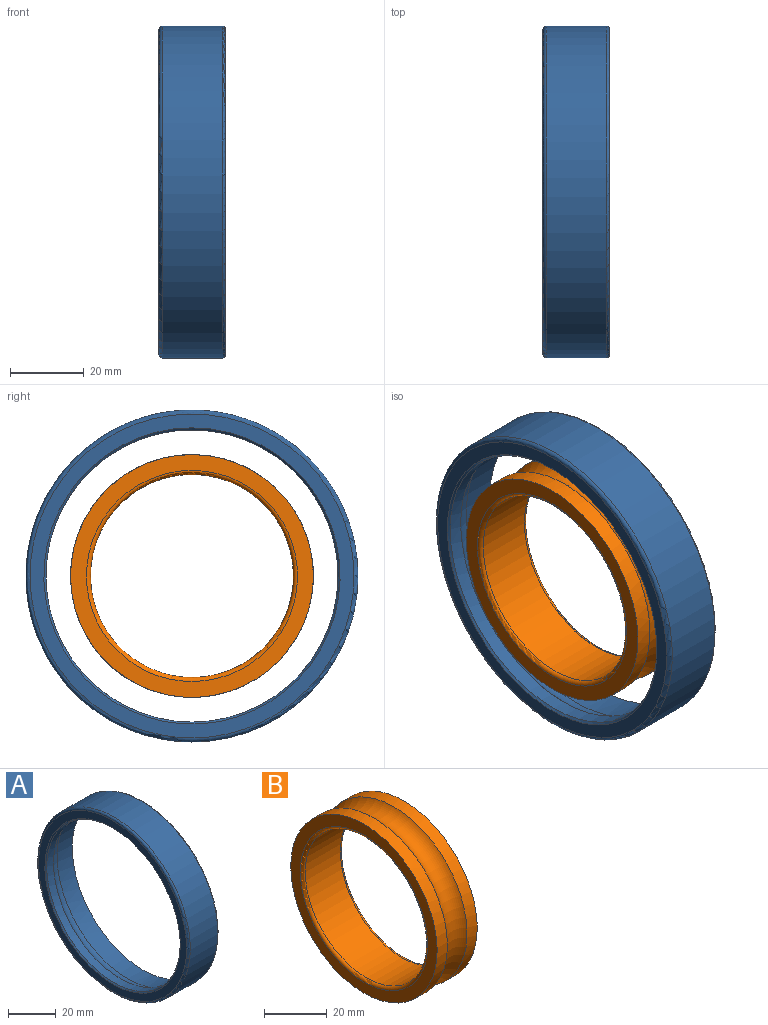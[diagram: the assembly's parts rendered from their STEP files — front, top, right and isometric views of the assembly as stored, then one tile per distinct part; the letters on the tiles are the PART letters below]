
ASSEMBLY  parts=2 mates=1
PART A: 9 faces, bbox 18x97.4x97.4 mm
  f0: plane 88.8x88.8mm, normal (1,0,0), area 664.1mm2, adj f1,f2
  f1: cone r=0mm half-angle=0.8deg, axis (1,0,0), area 2389.9mm2, adj f0,f3
  f2: torus R=44.4mm, axis (1,0,0), area 265.2mm2, adj f0,f4
  f3: torus R=36.26mm, axis (1,0,0), area 1307.1mm2, adj f1,f5
  f4: cylinder r=45mm len=90mm, axis (1,0,0), area 4608.7mm2, adj f2,f6
  f5: cylinder r=39.6mm len=79.2mm, axis (1,0,0), area 997.1mm2, adj f3,f7
  f6: torus R=43.9mm, axis (1,0,0), area 484.2mm2, adj f4,f8
  f7: cone r=0mm half-angle=45deg, axis (-1,0,0), area 194.9mm2, adj f5,f8
  f8: plane 87.8x87.8mm, normal (-1,0,0), area 990.7mm2, adj f6,f7
PART B: 8 faces, bbox 18x78.5x78.5 mm
  f0: torus R=28.6mm, axis (1,0,0), area 302.9mm2, adj f1,f2
  f1: cylinder r=27.5mm len=55mm, axis (1,0,0), area 2730mm2, adj f0,f3
  f2: plane 65.8x65.8mm, normal (-1,0,0), area 830.6mm2, adj f0,f4
  f3: torus R=28.6mm, axis (1,0,0), area 302.9mm2, adj f1,f5
  f4: cylinder r=32.9mm len=65.8mm, axis (1,0,0), area 946.3mm2, adj f2,f7
  f5: plane 65.8x65.8mm, normal (1,0,0), area 831mm2, adj f3,f6
  f6: cylinder r=32.9mm len=65.8mm, axis (1,0,0), area 946.3mm2, adj f5,f7
  f7: torus R=36.26mm, axis (1,0,0), area 2022mm2, adj f4,f6
PLACE A at identity fixed
PLACE B rot(axis=(-1,0,0),52.4deg) t=(0,0,0)mm
MATE revolute A.f1 <-> B.f0  axis (1,0,0) through (18,0,0)mm
